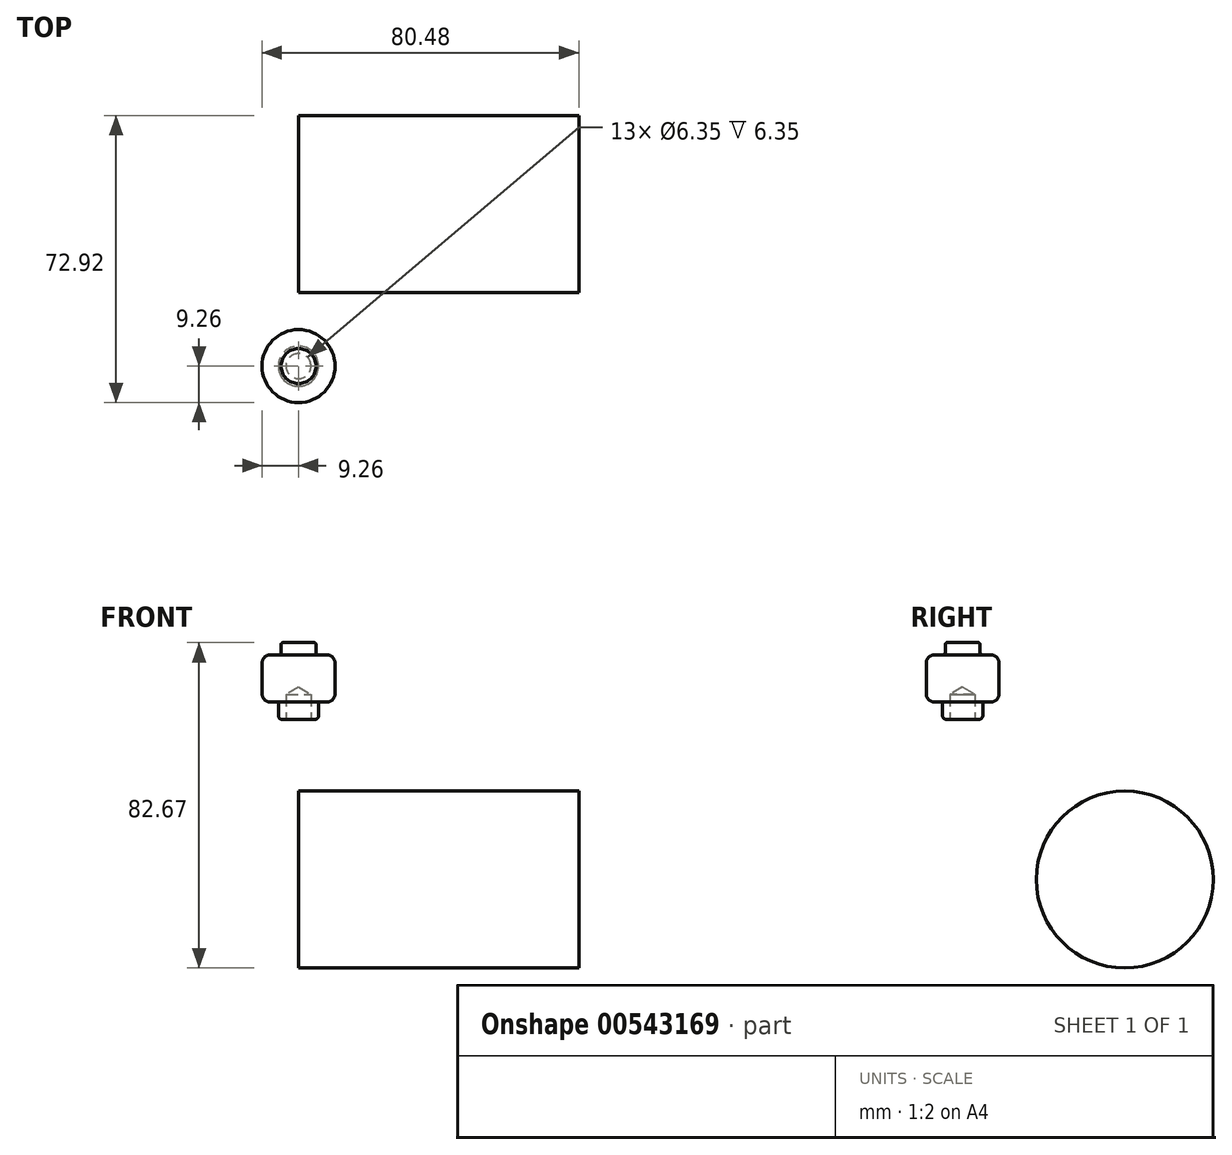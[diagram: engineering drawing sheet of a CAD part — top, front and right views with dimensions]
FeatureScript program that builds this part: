
annotation { "Feature Type Name" : "Feature", "Feature Type Description" : "" }
export const myFeature = defineFeature(function(context is Context, id is Id, definition is map)
    precondition{}
    {
        {
            var Q0;
            Q0=qCreatedBy(makeId("Front.planeOp"),FACE);
            var sketch = newSketch(context, id + "F0", { "sketchPlane" : qUnion([Q0])});
            skLineSegment(sketch, "E0", {"start": v(0, 19.52) * mm, "end": v(4.43, 19.52) * mm});
            skLineSegment(sketch, "E1", {"start": v(4.43, 19.52) * mm, "end": v(4.43, 16.44) * mm});
            skLineSegment(sketch, "E2", {"start": v(4.43, 16.44) * mm, "end": v(9.26, 16.44) * mm});
            skLineSegment(sketch, "E3", {"start": v(9.26, 16.44) * mm, "end": v(9.26, 4.4) * mm});
            skLineSegment(sketch, "E4", {"start": v(9.26, 4.4) * mm, "end": v(5.12, 4.4) * mm});
            skLineSegment(sketch, "E5", {"start": v(5.12, 4.4) * mm, "end": v(5.12, 0) * mm});
            skLineSegment(sketch, "E6", {"start": v(5.12, 0) * mm, "end": v(0, 0) * mm});
            skLineSegment(sketch, "E7", {"start": v(0, 0) * mm, "end": v(0, 19.52) * mm});
            skSolve(sketch);
        }
        {
            var Q0;
            Q0=makeQuery(id+"F0.imprint","IMPRINT",FACE,{"disambiguationData":[TD([[makeQuery(id+"F0.imprint","IMPRINT",EDGE,{"derivedFrom":sQuery(id+"F0.wireOp",EDGE,"E0")}),-1.0]])]});
            var Q1;
            Q1=sQuery(id+"F0.wireOp",EDGE,"E7");
            revolve(context, id + "F1", {"entities" : qUnion([Q0]), "axis" : qUnion([Q1]), "revolveType" : RevolveType.FULL});
        }
        {
            var Q0;
            Q0=makeQuery(id+"F1.opRevolve","SWEPT_EDGE",EDGE,{"disambiguationData":[OSD([sQuery(id+"F0.wireOp",EDGE,"E2"),sQuery(id+"F0.wireOp",EDGE,"E3")])]});
            var Q1;
            Q1=makeQuery(id+"F1.opRevolve","SWEPT_FACE",FACE,{"disambiguationData":[OSD([sQuery(id+"F0.wireOp",EDGE,"E3")])]});
            fillet(context, id + "F2", {"entities" : qUnion([Q0, Q1]), "radius" : 2.15 * mm, "tangentPropagation" : true, "allowEdgeOverflow" : false});
        }
        {
            var Q0;
            Q0=qCreatedBy(makeId("Right.planeOp"),FACE);
            var sketch = newSketch(context, id + "F3", { "sketchPlane" : qUnion([Q0])});
            skCircle(sketch, "E8", {"center": v(41.2, -40.68) * mm, "radius": 22.47 * mm});
            skSolve(sketch);
        }
        {
            var Q0;
            Q0=makeQuery(id+"F1.opRevolve","SWEPT_EDGE",EDGE,{"disambiguationData":[OSD([sQuery(id+"F0.wireOp",EDGE,"E0"),sQuery(id+"F0.wireOp",EDGE,"E1")])]});
            var Q1;
            Q1=makeQuery(id+"F1.opRevolve","SWEPT_FACE",FACE,{"disambiguationData":[OSD([sQuery(id+"F0.wireOp",EDGE,"E1")])]});
            fillet(context, id + "F4", {"entities" : qUnion([Q0, Q1]), "radius" : 0.5 * mm, "tangentPropagation" : true, "allowEdgeOverflow" : false});
        }
        {
            var Q0;
            Q0=makeQuery(id+"F1.opRevolve","SWEPT_FACE",FACE,{"disambiguationData":[OSD([sQuery(id+"F0.wireOp",EDGE,"E6")])]});
            var sketch = newSketch(context, id + "F5", { "sketchPlane" : qUnion([Q0])});
            skCircle(sketch, "E9", {"center": v(0, 0) * mm, "radius": 4.43 * mm});
            skSolve(sketch);
        }
        {
            var Q0;
            Q0=sQuery(id+"F5.wireOp",VERTEX,"E9.center");
            var Q1;
            Q1=makeQuery(id+"F1.opRevolve","SWEPT_BODY",BODY,{"disambiguationData":[OSD([sQuery(id+"F0.wireOp",EDGE,"E0"),sQuery(id+"F0.wireOp",EDGE,"E1"),sQuery(id+"F0.wireOp",EDGE,"E2"),sQuery(id+"F0.wireOp",EDGE,"E3"),sQuery(id+"F0.wireOp",EDGE,"E4"),sQuery(id+"F0.wireOp",EDGE,"E5"),sQuery(id+"F0.wireOp",EDGE,"E6"),sQuery(id+"F0.wireOp",EDGE,"E7")])]});
            hole(context, id + "F6", {"style" : HoleStyle.SIMPLE, "endStyle" : HoleEndStyle.BLIND, "holeDiameter" : 6.35 * mm, "holeDepth" : 6.35 * mm, "isTappedThrough" : true, "tappedDepth" : 12.7 * mm, "tapClearance" : 3, "locations" : qUnion([Q0]), "scope" : qUnion([Q1])});
        }
        {
            var Q0;
            Q0=makeQuery(id+"F1.opRevolve","SWEPT_EDGE",EDGE,{"disambiguationData":[OSD([sQuery(id+"F0.wireOp",EDGE,"E3"),sQuery(id+"F0.wireOp",EDGE,"E4")])]});
            var Q1;
            Q1=makeQuery(id+"F1.opRevolve","SWEPT_EDGE",EDGE,{"disambiguationData":[OSD([sQuery(id+"F0.wireOp",EDGE,"E5"),sQuery(id+"F0.wireOp",EDGE,"E6")])]});
            var Q2;
            {var subQ0=sQuery(id+"F0.wireOp",EDGE,"E3");Q2=makeQuery(id+"F2.opFillet","BLEND_EDGE",EDGE,{"blendedFrom":[makeQuery(id+"F1.opRevolve","SWEPT_EDGE",EDGE,{"disambiguationData":[OSD([sQuery(id+"F0.wireOp",EDGE,"E2"),subQ0])]}),makeQuery(id+"F1.opRevolve","SWEPT_FACE",FACE,{"disambiguationData":[OSD([subQ0])]})],"blendedInto":[makeQuery(id+"F1.opRevolve","SWEPT_FACE",FACE,{"disambiguationData":[OSD([subQ0])]})]});}
            var Q3;
            {var subQ0=sQuery(id+"F0.wireOp",EDGE,"E1");Q3=makeQuery(id+"F4.opFillet","BLEND_EDGE",EDGE,{"blendedFrom":[makeQuery(id+"F1.opRevolve","SWEPT_EDGE",EDGE,{"disambiguationData":[OSD([sQuery(id+"F0.wireOp",EDGE,"E0"),subQ0])]}),makeQuery(id+"F1.opRevolve","SWEPT_FACE",FACE,{"disambiguationData":[OSD([subQ0])]})],"blendedInto":[makeQuery(id+"F1.opRevolve","SWEPT_FACE",FACE,{"disambiguationData":[OSD([subQ0])]})]});}
            fillet(context, id + "F7", {"entities" : qUnion([Q0, Q1, Q2, Q3]), "radius" : 1.02 * mm, "tangentPropagation" : true, "allowEdgeOverflow" : false});
        }
        {
            var Q0;
            Q0=makeQuery(id+"F3.imprint","IMPRINT",FACE,{"disambiguationData":[TD([[makeQuery(id+"F3.imprint","IMPRINT",EDGE,{"derivedFrom":sQuery(id+"F3.wireOp",EDGE,"E8")}),1.0]])]});
            extrude(context, id + "F8", {"entities" : qUnion([Q0]), "depth" : 71.22 * mm, "offsetDistance" : 25.4 * mm});
        }
    });
